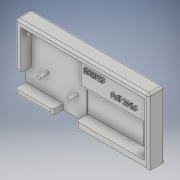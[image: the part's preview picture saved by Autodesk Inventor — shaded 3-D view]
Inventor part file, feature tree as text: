
AUTODESK INVENTOR PART (.ipt)
format: ipt  version: 2017 (Build 210142000, 142)  size: 583,680 bytes
history: native  units: in
note: dims shown in document units (in); Inventor stores cm internally (conversion verified against a paired STEP export)
features: extrude x10, sketch x10, fillet x4
ambient origin geometry x8: Origin, YZ Plane, XZ Plane, XY Plane, X Axis, Y Axis, Z Axis, Center Point
bodies: Solid1 (feature_tree)
feature tree (24):
  extrude  "Extrusion1"  Depth=2.4409in
  extrude  "Extrusion2"  Depth=0.5906in
  extrude  "Extrusion3"  Depth=0.3937in TaperAngle=0.0deg
  extrude  "Extrusion4"  Depth=0.0787in
  extrude  "Extrusion5"  Depth=0.3937in TaperAngle=0.0deg
  extrude  "Extrusion6"  Depth=0.5906in TaperAngle=0.0deg
  extrude  "Extrusion7"  Depth=1.9685in
  extrude  "Extrusion8"  Depth=0.1181in
  extrude  "Extrusion9"  Depth=0.1181in
  extrude  "Extrusion10"  Depth=0.3937in TaperAngle=0.0deg
  fillet  "Fillet1"  Radius=1.4567in
  fillet  "Fillet2"  Radius=0.3937in
  fillet  "Fillet3"  Radius=0.1181in
  fillet  "Fillet4"  Radius=0.0591in
  sketch  "Sketch3"  dims[d0=4.9213in d1=2.4409in]
  sketch  "Sketch4"  dims[d2=0.5906in d3=0.0in d4=2.0472in]
  sketch  "Sketch5"  dims[d5=2.0472in d7=0.3937in d8=0.0in]
  sketch  "Sketch6"  dims[d9=0.0787in d10=2.5197in]
  sketch  "Sketch7"  dims[d11=1.0433in d12=0.3937in d13=0.0in]
  sketch  "Sketch8"  dims[d14=0.4724in d15=0.5906in d16=0.0in]
  sketch  "Sketch9"  dims[d17=0.4331in d18=0.0in d19=1.9685in]
  sketch  "Sketch10"  dims[d20=1.9685in d28=0.1181in]
  sketch  "Sketch13"  dims[d29=0.1181in d30=0.1181in]
  sketch  "Sketch14"  dims[d31=0.315in d32=0.0in d34=0.3937in d35=0.0in d36=1.4567in d37=0.3937in d38=0.0in d39=0.1181in d40=0.0in d41=0.0591in d42=0.0in d43=0.0787in d44=0.0787in d45=0.0787in d46=0.0787in]
